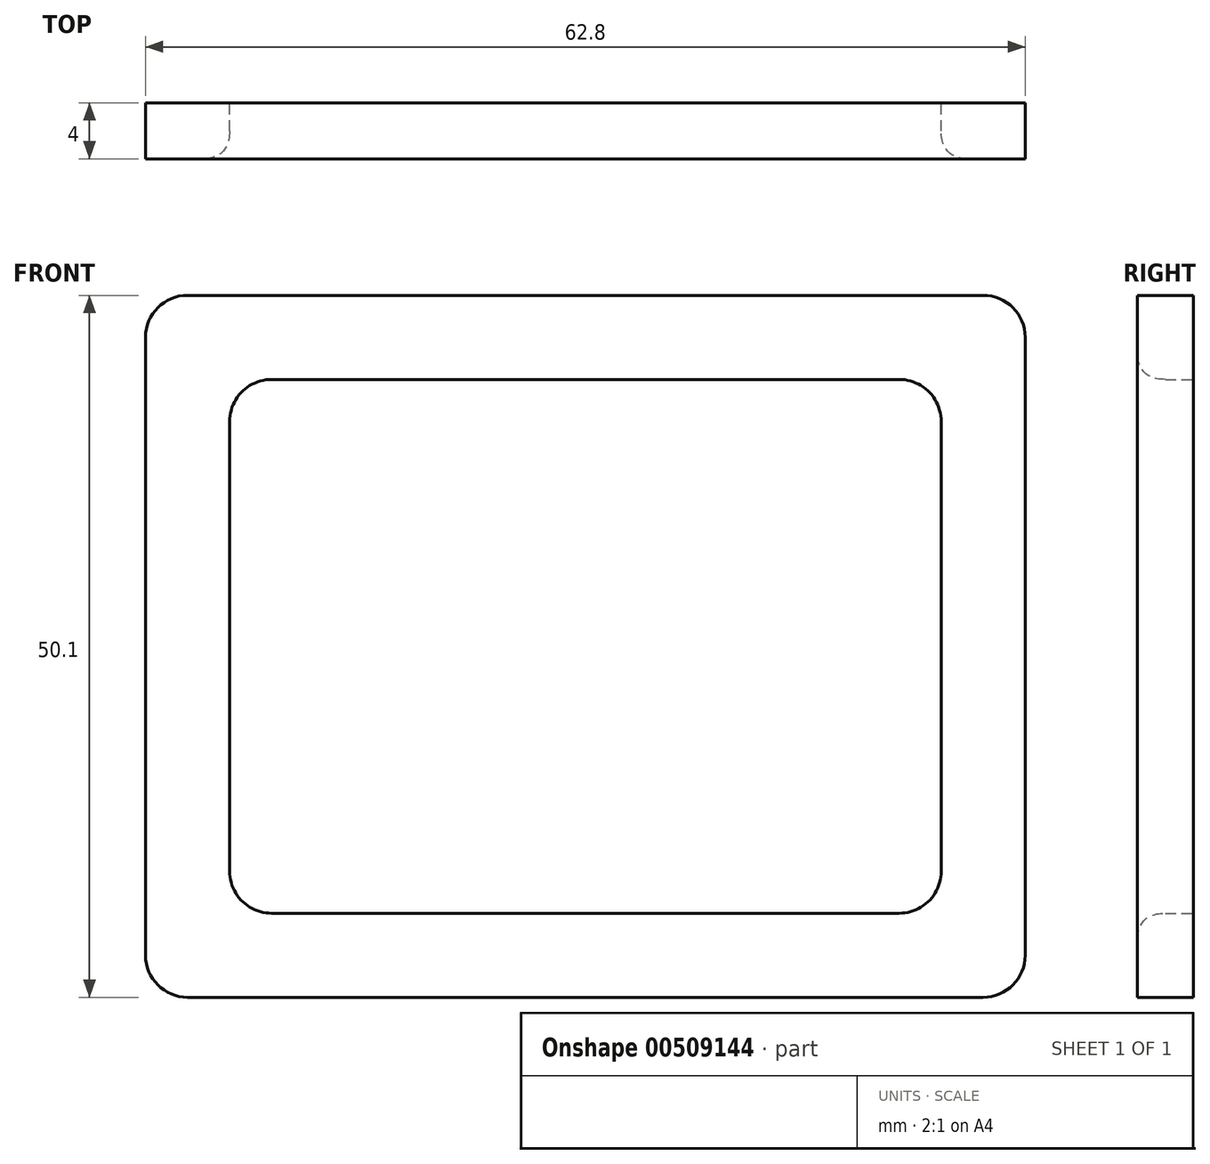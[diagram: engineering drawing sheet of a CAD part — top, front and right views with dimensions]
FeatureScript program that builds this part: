
annotation { "Feature Type Name" : "Feature", "Feature Type Description" : "" }
export const myFeature = defineFeature(function(context is Context, id is Id, definition is map)
    precondition{}
    {
        {
            var Q0;
            Q0=qCreatedBy(makeId("Front.planeOp"),FACE);
            var sketch = newSketch(context, id + "F0", { "sketchPlane" : qUnion([Q0])});
            skLineSegment(sketch, "E0.bottom", {"start": v(-197.16, 50.67) * mm, "end": v(-152.36, 50.67) * mm});
            skLineSegment(sketch, "E0.top", {"start": v(-197.16, 12.57) * mm, "end": v(-152.36, 12.57) * mm});
            skLineSegment(sketch, "E0.left", {"start": v(-200.16, 47.67) * mm, "end": v(-200.16, 15.57) * mm});
            skLineSegment(sketch, "E0.right", {"start": v(-149.36, 47.67) * mm, "end": v(-149.36, 15.57) * mm});
            skLineSegment(sketch, "E1.bottom", {"start": v(-203.16, 56.67) * mm, "end": v(-146.36, 56.67) * mm});
            skLineSegment(sketch, "E1.top", {"start": v(-203.16, 6.57) * mm, "end": v(-146.36, 6.57) * mm});
            skLineSegment(sketch, "E1.left", {"start": v(-206.16, 53.67) * mm, "end": v(-206.16, 9.57) * mm});
            skLineSegment(sketch, "E1.right", {"start": v(-143.36, 53.67) * mm, "end": v(-143.36, 9.57) * mm});
            skPoint(sketch, "E2.visualSharp", {"position": v(-200.16, 50.67) * mm});
            skArc(sketch, "E2.filletArc", {"start": v(-197.16, 50.67) * mm, "mid": v(-199.28, 49.8) * mm, "end": v(-200.16, 47.67) * mm});
            skPoint(sketch, "E3.visualSharp", {"position": v(-149.36, 50.67) * mm});
            skArc(sketch, "E3.filletArc", {"start": v(-149.36, 47.67) * mm, "mid": v(-150.24, 49.8) * mm, "end": v(-152.36, 50.67) * mm});
            skPoint(sketch, "E4.visualSharp", {"position": v(-149.36, 12.57) * mm});
            skArc(sketch, "E4.filletArc", {"start": v(-152.36, 12.57) * mm, "mid": v(-150.24, 13.45) * mm, "end": v(-149.36, 15.57) * mm});
            skPoint(sketch, "E5.visualSharp", {"position": v(-200.16, 12.57) * mm});
            skArc(sketch, "E5.filletArc", {"start": v(-200.16, 15.57) * mm, "mid": v(-199.28, 13.45) * mm, "end": v(-197.16, 12.57) * mm});
            skPoint(sketch, "E6.visualSharp", {"position": v(-206.16, 56.67) * mm});
            skArc(sketch, "E6.filletArc", {"start": v(-203.16, 56.67) * mm, "mid": v(-205.28, 55.8) * mm, "end": v(-206.16, 53.67) * mm});
            skPoint(sketch, "E7.visualSharp", {"position": v(-143.36, 56.67) * mm});
            skArc(sketch, "E7.filletArc", {"start": v(-143.36, 53.67) * mm, "mid": v(-144.24, 55.8) * mm, "end": v(-146.36, 56.67) * mm});
            skPoint(sketch, "E8.visualSharp", {"position": v(-143.36, 6.57) * mm});
            skArc(sketch, "E8.filletArc", {"start": v(-146.36, 6.57) * mm, "mid": v(-144.24, 7.45) * mm, "end": v(-143.36, 9.57) * mm});
            skPoint(sketch, "E9.visualSharp", {"position": v(-206.16, 6.57) * mm});
            skArc(sketch, "E9.filletArc", {"start": v(-206.16, 9.57) * mm, "mid": v(-205.28, 7.45) * mm, "end": v(-203.16, 6.57) * mm});
            skSolve(sketch);
        }
        {
            var Q0;
            Q0=makeQuery(id+"F0.imprint","IMPRINT",FACE,{"disambiguationData":[TD([[makeQuery(id+"F0.imprint","IMPRINT",EDGE,{"derivedFrom":sQuery(id+"F0.wireOp",EDGE,"E0.bottom")}),1.0]])]});
            var Q1;
            Q1=makeQuery(id+"F0.imprint","IMPRINT",FACE,{"disambiguationData":[TD([[makeQuery(id+"F0.imprint","IMPRINT",EDGE,{"derivedFrom":sQuery(id+"F0.wireOp",EDGE,"a1ded7ab-1fbd-4a69-913e-5210085afb6b.bottom")}),1.0]])]});
            extrude(context, id + "F1", {"entities" : qUnion([Q0, Q1]), "depth" : 4 * mm, "offsetDistance" : 25 * mm});
        }
        {
            var Q0;
            Q0=makeQuery(id+"F1.opExtrude","CAP_EDGE",EDGE,{"disambiguationData":[OSD([sQuery(id+"F0.wireOp",EDGE,"E0.left")])],"isStart":false});
            fillet(context, id + "F2", {"entities" : qUnion([Q0]), "tangentPropagation" : true, "crossSection" : FilletCrossSection.CONIC, "radius" : 2 * mm, "rho" : 0.5, "defaultsChanged" : false, "vertexSettings" : [], "allowEdgeOverflow" : false});
        }
    });
